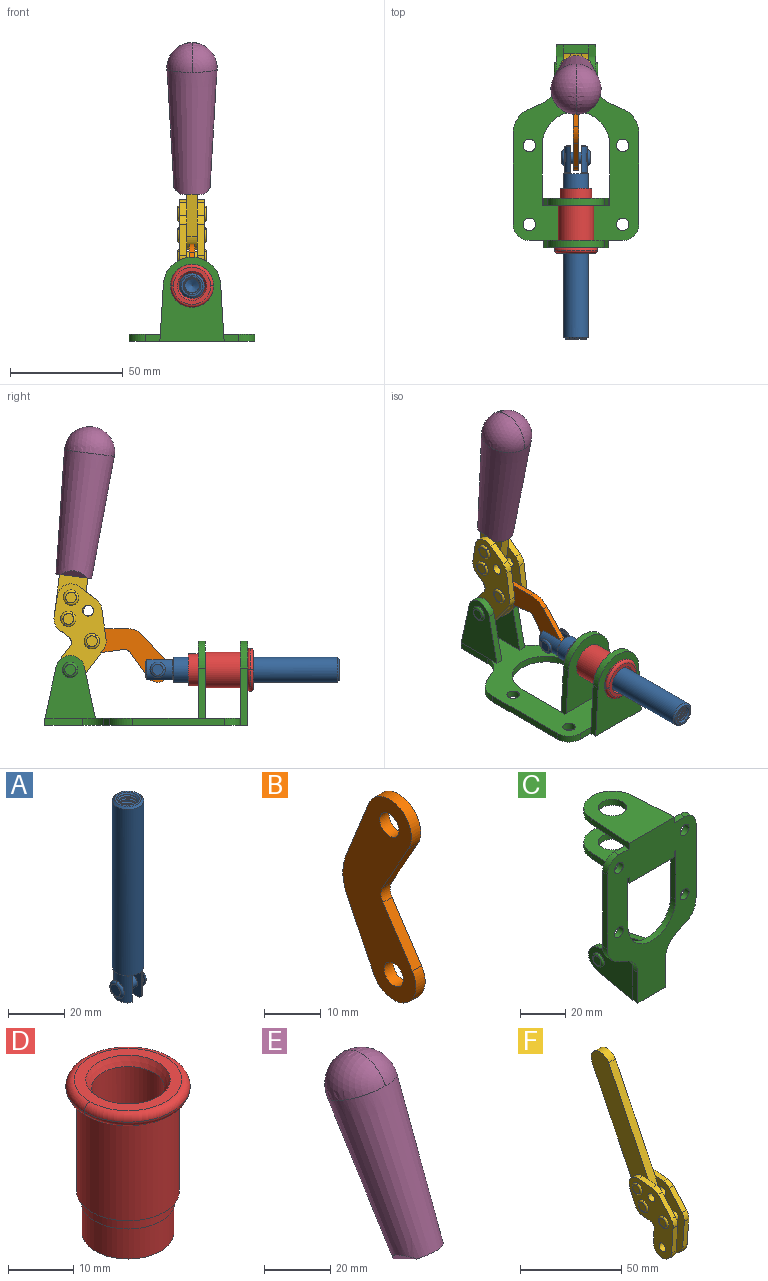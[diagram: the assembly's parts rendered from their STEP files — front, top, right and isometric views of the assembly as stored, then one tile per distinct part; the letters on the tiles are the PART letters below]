
ASSEMBLY  parts=6 mates=6
PART A: 48 faces, bbox 12.6x11.1x86.1 mm
  f0: torus R=2.41mm, axis (-1,0,0), area 15mm2, adj f30,f32,f34
  f1: torus R=2.41mm, axis (-1,0,0), area 15mm2, adj f29,f31,f33
  f2: cylinder r=5.54mm len=72.39mm, axis (0,0,1), area 2518.5mm2, adj f3,f4,f42,f43
  f3: cone r=5.54mm half-angle=45deg, axis (0,0,1), area 7.6mm2, adj f2,f5,f41
  f4: cone r=5.54mm half-angle=45deg, axis (0,0,-1), area 34.9mm2, adj f2,f39
  f5: cylinder r=5.08mm len=11.48mm, axis (0,0,1), area 108.3mm2, adj f3,f7,f8,f41
  f6: cylinder r=2.41mm len=4.83mm, axis (-1,0,0), area 71.2mm2, adj f40,f41
  f7: cylinder r=2.41mm len=4.83mm, axis (-1,0,0), area 7.6mm2, adj f5,f34
  f8: cone r=5.08mm half-angle=45deg, axis (0,0,1), area 10.6mm2, adj f5,f37,f41
  f9: cone r=3.98mm half-angle=45deg, axis (0,0,1), area 17.6mm2, adj f27,f39,f45,f46,f47
  f10: cylinder r=2.41mm len=4.83mm, axis (-1,0,0), area 7.6mm2, adj f33,f38
  f11: cylinder r=3.2mm len=6.4mm, axis (0,0,1), area 78.4mm2, adj f12,f28,f44,f45,f47
  f12: cylinder r=3.2mm len=6.4mm, axis (0,0,1), area 10.5mm2, adj f11,f13,f45,f47
  f13: cylinder r=3.2mm len=6.4mm, axis (0,0,1), area 10.5mm2, adj f12,f14,f45,f47
  f14: cylinder r=3.2mm len=6.4mm, axis (0,0,1), area 10.5mm2, adj f13,f15,f45,f47
  f15: cylinder r=3.2mm len=6.4mm, axis (0,0,1), area 10.5mm2, adj f14,f16,f45,f47
  f16: cylinder r=3.2mm len=6.4mm, axis (0,0,1), area 10.5mm2, adj f15,f17,f45,f47
  f17: cylinder r=3.2mm len=6.4mm, axis (0,0,1), area 10.5mm2, adj f16,f18,f45,f47
  f18: cylinder r=3.2mm len=6.4mm, axis (0,0,1), area 10.5mm2, adj f17,f19,f45,f47
  f19: cylinder r=3.2mm len=6.4mm, axis (0,0,1), area 10.5mm2, adj f18,f20,f45,f47
  f20: cylinder r=3.2mm len=6.4mm, axis (0,0,1), area 10.5mm2, adj f19,f21,f45,f47
  f21: cylinder r=3.2mm len=6.4mm, axis (0,0,1), area 10.5mm2, adj f20,f22,f45,f47
  f22: cylinder r=3.2mm len=6.4mm, axis (0,0,1), area 10.5mm2, adj f21,f23,f45,f47
  f23: cylinder r=3.2mm len=6.4mm, axis (0,0,1), area 10.5mm2, adj f22,f24,f45,f47
  f24: cylinder r=3.2mm len=6.4mm, axis (0,0,1), area 10.5mm2, adj f23,f25,f45,f47
  f25: cylinder r=3.2mm len=6.4mm, axis (0,0,1), area 10.5mm2, adj f24,f26,f45,f47
  f26: cylinder r=3.2mm len=6.4mm, axis (0,0,1), area 10.5mm2, adj f25,f27,f45,f47
  f27: cylinder r=3.2mm len=6.4mm, axis (0,0,1), area 7.4mm2, adj f9,f26,f45,f47
  f28: cone r=3.2mm half-angle=60deg, axis (0,0,1), area 37.2mm2, adj f11
  f29: plane 4.83x4.83mm, normal (-1,0,0), area 18.3mm2, adj f1,f31
  f30: plane 4.83x4.83mm, normal (1,0,0), area 18.3mm2, adj f0,f32
  f31: torus R=2.41mm, axis (-1,0,0), area 15mm2, adj f1,f29,f33
  f32: torus R=2.41mm, axis (-1,0,0), area 15mm2, adj f0,f30,f34
  f33: plane 6.83x6.83mm, normal (1,0,0), area 18.3mm2, adj f1,f10,f31
  f34: plane 6.83x6.83mm, normal (-1,0,0), area 18.3mm2, adj f0,f7,f32
  f35: cone r=5.08mm half-angle=45deg, axis (0,0,1), area 10.6mm2, adj f36,f38,f40
  f36: plane 7.25x1.97mm, normal (0,0,-1), area 10mm2, adj f35,f40
  f37: plane 7.25x1.97mm, normal (0,0,-1), area 10mm2, adj f8,f41
  f38: cylinder r=5.08mm len=11.48mm, axis (0,0,1), area 108.3mm2, adj f10,f35,f40,f42
  f39: plane 9.55x9.55mm, normal (0,0,1), area 22mm2, adj f4,f9
  f40: plane 12.76x10.09mm, normal (1,0,0), area 95.7mm2, adj f6,f35,f36,f38,f42,f43
  f41: plane 12.76x10.09mm, normal (-1,0,0), area 95.7mm2, adj f3,f5,f6,f8,f37,f43
  f42: cone r=5.54mm half-angle=45deg, axis (0,0,1), area 7.6mm2, adj f2,f38,f40
  f43: plane 11.07x4.7mm, normal (0,0,-1), area 50.4mm2, adj f2,f40,f41
  f44: plane 0.89x0.62mm, normal (-1,0,0), area 0.3mm2, adj f11,f45,f46,f47
  f45: bspline ~24.8x7.63mm, area 266.6mm2, adj f9,f11,f12,f13,f14,f15,f16,f17
  f46: bspline ~24.87x7.63mm, area 73.6mm2, adj f9,f44,f45,f47
  f47: bspline ~24.98x7.63mm, area 272.5mm2, adj f9,f11,f12,f13,f14,f15,f16,f17
PART B: 12 faces, bbox 2.3x18.2x42.8 mm
  f0: cylinder r=2.4mm len=4.8mm, axis (1,0,0), area 34.9mm2, adj f4,f11
  f1: cylinder r=10.41mm len=8.47mm, axis (1,0,0), area 20.2mm2, adj f4,f9,f10,f11
  f2: cylinder r=3.05mm len=3.16mm, axis (1,0,0), area 7.7mm2, adj f4,f6,f7,f11
  f3: cylinder r=2.4mm len=4.8mm, axis (1,0,0), area 34.9mm2, adj f4,f11
  f4: plane 42.81x18.23mm, normal (-1,0,0), area 414.1mm2, adj f0,f1,f2,f3,f5,f6,f7,f8
  f5: cylinder r=5.54mm len=10.67mm, axis (1,0,0), area 41.8mm2, adj f4,f6,f10,f11
  f6: plane 11.66x6.53mm, normal (0,-0.87,-0.49), area 30.9mm2, adj f2,f4,f5,f11
  f7: plane 11.17x7.33mm, normal (0,-0.84,0.55), area 30.9mm2, adj f2,f4,f8,f11
  f8: cylinder r=5.54mm len=10.51mm, axis (1,0,0), area 41.8mm2, adj f4,f7,f9,f11
  f9: plane 13.67x6.67mm, normal (0,0.9,-0.44), area 35.1mm2, adj f1,f4,f8,f11
  f10: plane 14.1x5.7mm, normal (0,0.93,0.37), area 35.1mm2, adj f1,f4,f5,f11
  f11: plane 42.81x18.23mm, normal (1,0,0), area 414.1mm2, adj f0,f1,f2,f3,f5,f6,f7,f8
PART C: 55 faces, bbox 55.7x37.4x89.8 mm
  f0: torus R=2.41mm, axis (-1,0,0), area 15mm2, adj f11,f15,f25
  f1: torus R=2.41mm, axis (-1,0,0), area 15mm2, adj f10,f12,f22
  f2: cylinder r=2.78mm len=5.56mm, axis (0,-1,0), area 54.2mm2, adj f30,f54
  f3: cylinder r=14.99mm len=29.97mm, axis (0,-1,0), area 145.9mm2, adj f30,f49,f53,f54
  f4: cylinder r=2.78mm len=5.56mm, axis (0,-1,0), area 54.2mm2, adj f30,f54
  f5: cylinder r=2.78mm len=5.56mm, axis (0,-1,0), area 54.2mm2, adj f30,f54
  f6: cylinder r=2.78mm len=5.56mm, axis (0,-1,0), area 54.2mm2, adj f30,f54
  f7: cylinder r=6.35mm len=12.7mm, axis (0,0,1), area 123.6mm2, adj f27,f51
  f8: cylinder r=6.35mm len=12.7mm, axis (0,0,-1), area 124.7mm2, adj f21,f35
  f9: cylinder r=2.41mm len=11.18mm, axis (-1,0,0), area 169.4mm2, adj f16,f19
  f10: plane 4.83x4.83mm, normal (1,0,0), area 18.3mm2, adj f1,f12
  f11: plane 4.83x4.83mm, normal (-1,0,0), area 18.3mm2, adj f0,f15
  f12: torus R=2.41mm, axis (-1,0,0), area 15mm2, adj f1,f10,f22
  f13: cylinder r=6.35mm len=12.41mm, axis (1,0,0), area 53.4mm2, adj f18,f19,f22,f23
  f14: cylinder r=6.35mm len=12.41mm, axis (-1,0,0), area 53.4mm2, adj f16,f17,f24,f25
  f15: torus R=2.41mm, axis (-1,0,0), area 15mm2, adj f0,f11,f25
  f16: plane 27.86x22.35mm, normal (1,0,0), area 425.4mm2, adj f9,f14,f17,f24,f30
  f17: plane 22.86x4.97mm, normal (0,0.21,0.98), area 72.5mm2, adj f14,f16,f25,f30
  f18: plane 22.86x4.97mm, normal (0,0.21,0.98), area 72.5mm2, adj f13,f19,f22,f30
  f19: plane 27.86x22.35mm, normal (-1,0,0), area 425.4mm2, adj f9,f13,f18,f23,f30
  f20: cylinder r=12.7mm len=25.35mm, axis (0,0,-1), area 119.8mm2, adj f21,f34,f35,f36
  f21: plane 34.21x28.07mm, normal (0,0,-1), area 702.4mm2, adj f8,f20,f30,f34,f36
  f22: plane 27.96x22.45mm, normal (1,0,0), area 407.2mm2, adj f1,f12,f13,f18,f23,f30,f42,f43
  f23: plane 22.86x4.97mm, normal (0,0.21,-0.98), area 72.5mm2, adj f13,f19,f22,f44
  f24: plane 22.86x4.97mm, normal (0,0.21,-0.98), area 72.5mm2, adj f14,f16,f25,f44
  f25: plane 27.86x22.35mm, normal (-1,0,0), area 407.1mm2, adj f0,f14,f15,f17,f24,f30,f45,f46
  f26: plane 3.1x0.95mm, normal (0,0,-1), area 2.7mm2, adj f30,f49,f50,f54
  f27: plane 34.21x28.07mm, normal (0,0,1), area 702.4mm2, adj f7,f28,f30,f50,f52
  f28: cylinder r=12.7mm len=25.35mm, axis (0,0,1), area 118.8mm2, adj f27,f50,f51,f52
  f29: plane 3.1x0.95mm, normal (0,0,-1), area 2.7mm2, adj f30,f52,f53,f54
  f30: plane 86.54x55.63mm, normal (0,1,0), area 2362.9mm2, adj f2,f3,f4,f5,f6,f16,f17,f18
  f31: plane 40.56x3.1mm, normal (-1,0,0), area 125.7mm2, adj f30,f32,f48,f54
  f32: cylinder r=7.11mm len=7.11mm, axis (0,-1,0), area 34.6mm2, adj f30,f31,f33,f54
  f33: plane 6.67x3.1mm, normal (0,0,1), area 20.4mm2, adj f30,f32,f34,f54
  f34: plane 25.39x3.13mm, normal (-1,0.06,0), area 79.5mm2, adj f20,f21,f33,f35,f54
  f35: plane 37.31x28.45mm, normal (0,0,1), area 789.9mm2, adj f8,f20,f34,f36,f54
  f36: plane 25.39x3.13mm, normal (1,0.06,0), area 79.5mm2, adj f20,f21,f35,f37,f54
  f37: plane 6.67x3.1mm, normal (0,0,1), area 20.4mm2, adj f30,f36,f38,f54
  f38: cylinder r=7.11mm len=7.11mm, axis (0,-1,0), area 34.6mm2, adj f30,f37,f39,f54
  f39: plane 40.56x3.1mm, normal (1,0,0), area 125.7mm2, adj f30,f38,f40,f54
  f40: cylinder r=11.18mm len=10.16mm, axis (0,-1,0), area 39.5mm2, adj f30,f39,f41,f54
  f41: plane 6.09x3.1mm, normal (0.42,0,-0.91), area 20.8mm2, adj f30,f40,f42,f54
  f42: cylinder r=11.18mm len=9.41mm, axis (0,-1,0), area 37.2mm2, adj f22,f30,f41,f43,f54
  f43: plane 16.5x3.1mm, normal (1,0,0), area 51.1mm2, adj f22,f42,f44,f54
  f44: plane 17.37x3.1mm, normal (0,0,-1), area 53.8mm2, adj f23,f24,f30,f43,f45,f54
  f45: plane 16.5x3.1mm, normal (-1,0,0), area 51.1mm2, adj f25,f44,f46,f54
  f46: cylinder r=11.18mm len=9.41mm, axis (0,-1,0), area 37.2mm2, adj f25,f30,f45,f47,f54
  f47: plane 6.09x3.1mm, normal (-0.42,0,-0.91), area 20.8mm2, adj f30,f46,f48,f54
  f48: cylinder r=11.18mm len=10.16mm, axis (0,-1,0), area 39.5mm2, adj f30,f31,f47,f54
  f49: plane 26.54x3.1mm, normal (-1,0,0), area 82.3mm2, adj f3,f26,f30,f54
  f50: plane 25.39x3.1mm, normal (1,0.06,0), area 78.8mm2, adj f26,f27,f28,f51,f54
  f51: plane 37.31x28.45mm, normal (0,0,-1), area 789.9mm2, adj f7,f28,f50,f52,f54
  f52: plane 25.39x3.1mm, normal (-1,0.06,0), area 78.8mm2, adj f27,f28,f29,f51,f54
  f53: plane 26.54x3.1mm, normal (1,0,0), area 82.3mm2, adj f3,f29,f30,f54
  f54: plane 89.66x55.63mm, normal (0,-1,0), area 2678.5mm2, adj f2,f3,f4,f5,f6,f26,f29,f31
PART D: 15 faces, bbox 20.6x20.6x28.7 mm
  f0: torus R=8.26mm, axis (0,0,1), area 56.8mm2, adj f1,f10,f12
  f1: torus R=8.26mm, axis (0,0,1), area 56.8mm2, adj f0,f6,f13
  f2: cylinder r=5.59mm len=25.91mm, axis (0,0,1), area 909.6mm2, adj f3,f4
  f3: cone r=6.86mm half-angle=45deg, axis (0,0,-1), area 70.2mm2, adj f2,f14
  f4: cone r=6.47mm half-angle=30deg, axis (0,0,1), area 66.7mm2, adj f2,f13
  f5: cylinder r=7.04mm len=14.07mm, axis (0,0,1), area 252.6mm2, adj f11,f14
  f6: torus R=8.26mm, axis (0,0,1), area 56.8mm2, adj f1,f12,f13
  f7: cylinder r=7.16mm len=14.33mm, axis (0,0,1), area 91.5mm2, adj f9,f11
  f8: cylinder r=7.86mm len=18.42mm, axis (0,0,1), area 909.6mm2, adj f9,f10
  f9: plane 15.72x15.72mm, normal (0,0,-1), area 33mm2, adj f7,f8
  f10: plane 16.51x16.51mm, normal (0,0,-1), area 19.9mm2, adj f0,f8,f12
  f11: plane 14.33x14.33mm, normal (0,0,-1), area 5.7mm2, adj f5,f7
  f12: torus R=8.26mm, axis (0,0,1), area 56.8mm2, adj f0,f6,f10
  f13: plane 16.51x16.51mm, normal (0,0,1), area 82.7mm2, adj f1,f4,f6
  f14: plane 14.07x14.07mm, normal (0,0,-1), area 7.8mm2, adj f3,f5
PART E: 11 faces, bbox 22.3x42.6x64.5 mm
  f0: sphere r=11.13mm, area 411.4mm2, adj f1,f8
  f1: cone r=11.11mm half-angle=3.3deg, axis (0,0.44,0.9), area 3251.8mm2, adj f0,f7,f8,f9,f10
  f2: cylinder r=6.16mm len=11.7mm, axis (1,0,0), area 89.5mm2, adj f3,f4,f5,f6
  f3: plane 60.23x36.75mm, normal (-1,0,0), area 763.6mm2, adj f2,f4,f6,f10
  f4: plane 51.37x25.05mm, normal (0,0.9,-0.44), area 264.2mm2, adj f2,f3,f5,f10
  f5: plane 60.23x36.75mm, normal (1,0,0), area 763.6mm2, adj f2,f4,f6,f10
  f6: plane 51.37x25.05mm, normal (0,-0.9,0.44), area 264.2mm2, adj f2,f3,f5,f10
  f7: plane 9.95x5.95mm, normal (0.71,-0.31,-0.64), area 25.8mm2, adj f1,f10
  f8: sphere r=11.13mm, area 411.4mm2, adj f0,f1
  f9: plane 9.95x5.95mm, normal (-0.71,-0.31,-0.64), area 25.8mm2, adj f1,f10
  f10: plane 14.27x11.38mm, normal (0,-0.44,-0.9), area 106.7mm2, adj f1,f3,f4,f5,f6,f7,f9
PART F: 59 faces, bbox 12.9x60.2x99.6 mm
  f0: torus R=2.39mm, axis (-1,0,0), area 14.9mm2, adj f20,f43,f51
  f1: torus R=2.39mm, axis (-1,0,0), area 14.9mm2, adj f19,f42,f51
  f2: torus R=2.39mm, axis (-1,0,0), area 14.9mm2, adj f18,f35,f51
  f3: torus R=2.39mm, axis (-1,0,0), area 14.9mm2, adj f14,f17,f23
  f4: torus R=2.39mm, axis (-1,0,0), area 14.9mm2, adj f13,f16,f23
  f5: torus R=2.39mm, axis (-1,0,0), area 14.9mm2, adj f12,f15,f23
  f6: cylinder r=2.39mm len=4.78mm, axis (1,0,0), area 46.5mm2, adj f48,f50,f51
  f7: cylinder r=2.39mm len=4.78mm, axis (1,0,0), area 46.5mm2, adj f50,f51
  f8: cylinder r=6.35mm len=12.68mm, axis (1,0,0), area 61.8mm2, adj f38,f39,f50,f51
  f9: cylinder r=2.39mm len=4.78mm, axis (-1,0,0), area 70.5mm2, adj f46,f50
  f10: cylinder r=2.39mm len=4.78mm, axis (-1,0,0), area 46.5mm2, adj f23,f45,f46
  f11: cylinder r=2.39mm len=4.78mm, axis (-1,0,0), area 46.5mm2, adj f23,f46
  f12: plane 4.78x4.78mm, normal (1,0,0), area 17.9mm2, adj f5,f15
  f13: plane 4.78x4.78mm, normal (1,0,0), area 17.9mm2, adj f4,f16
  f14: plane 4.78x4.78mm, normal (1,0,0), area 17.9mm2, adj f3,f17
  f15: torus R=2.39mm, axis (-1,0,0), area 14.9mm2, adj f5,f12,f23
  f16: torus R=2.39mm, axis (-1,0,0), area 14.9mm2, adj f4,f13,f23
  f17: torus R=2.39mm, axis (-1,0,0), area 14.9mm2, adj f3,f14,f23
  f18: plane 4.78x4.78mm, normal (-1,0,0), area 17.9mm2, adj f2,f35
  f19: plane 4.78x4.78mm, normal (-1,0,0), area 17.9mm2, adj f1,f42
  f20: plane 4.78x4.78mm, normal (-1,0,0), area 17.9mm2, adj f0,f43
  f21: plane 2.26x0.2mm, normal (1,0,0), area 0.2mm2, adj f31,f44
  f22: plane 2.26x0.2mm, normal (-1,0,0), area 0.2mm2, adj f41,f44
  f23: plane 39.37x30.77mm, normal (1,0,0), area 565.5mm2, adj f3,f4,f5,f10,f11,f15,f16,f17
  f24: cylinder r=6.1mm len=4.15mm, axis (-1,0,0), area 14.7mm2, adj f23,f25,f32,f46
  f25: plane 10.25x9.01mm, normal (0,-0.75,0.66), area 42.3mm2, adj f23,f24,f26,f46
  f26: cylinder r=6.35mm len=4.64mm, axis (-1,0,0), area 15.6mm2, adj f23,f25,f27,f46
  f27: plane 15.84x3.1mm, normal (0,-1,-0.07), area 49.2mm2, adj f23,f26,f28,f46
  f28: cylinder r=6.35mm len=12.68mm, axis (-1,0,0), area 61.8mm2, adj f23,f27,f29,f46
  f29: plane 8.11x3.1mm, normal (0,1,0.07), area 25.2mm2, adj f23,f28,f30,f46
  f30: cylinder r=3.05mm len=3.25mm, axis (-1,0,0), area 14.8mm2, adj f23,f29,f31,f46
  f31: plane 5.99x3.1mm, normal (0,0.07,-1), area 18.6mm2, adj f21,f23,f30,f44,f46
  f32: plane 9.5x3.1mm, normal (0,-0.07,1), area 29.5mm2, adj f23,f24,f33,f46,f47
  f33: cylinder r=6.1mm len=8.63mm, axis (-1,0,0), area 39.1mm2, adj f23,f32,f34,f47
  f34: plane 8.65x3.96mm, normal (0,0.91,-0.42), area 29.5mm2, adj f23,f33,f44,f47
  f35: torus R=2.39mm, axis (-1,0,0), area 14.9mm2, adj f2,f18,f51
  f36: plane 10.25x9.01mm, normal (0,-0.75,0.66), area 42.3mm2, adj f37,f49,f50,f51
  f37: cylinder r=6.35mm len=4.64mm, axis (1,0,0), area 15.6mm2, adj f36,f38,f50,f51
  f38: plane 15.84x3.1mm, normal (0,-1,-0.07), area 49.2mm2, adj f8,f37,f50,f51
  f39: plane 8.11x3.1mm, normal (0,1,0.07), area 25.2mm2, adj f8,f40,f50,f51
  f40: cylinder r=3.05mm len=3.25mm, axis (1,0,0), area 14.8mm2, adj f39,f41,f50,f51
  f41: plane 5.99x3.1mm, normal (0,0.07,-1), area 18.6mm2, adj f22,f40,f44,f50,f51
  f42: torus R=2.39mm, axis (-1,0,0), area 14.9mm2, adj f1,f19,f51
  f43: torus R=2.39mm, axis (-1,0,0), area 14.9mm2, adj f0,f20,f51
  f44: cylinder r=6.35mm len=12.12mm, axis (-1,0,0), area 128.9mm2, adj f21,f22,f23,f31,f34,f41,f46,f47
  f45: plane 2.65x1.35mm, normal (1,0,0), area 1mm2, adj f10,f55
  f46: plane 39.08x20.42mm, normal (-1,0,0), area 412.5mm2, adj f9,f10,f11,f24,f25,f26,f27,f28
  f47: plane 77.62x39.82mm, normal (1,0,0), area 850mm2, adj f32,f33,f34,f44,f53,f54,f55
  f48: plane 2.65x1.35mm, normal (-1,0,0), area 1mm2, adj f6,f55
  f49: cylinder r=6.1mm len=4.15mm, axis (1,0,0), area 14.7mm2, adj f36,f50,f51,f56
  f50: plane 39.08x20.42mm, normal (1,0,0), area 412.5mm2, adj f6,f7,f8,f9,f36,f37,f38,f39
  f51: plane 39.37x30.77mm, normal (-1,0,0), area 565.5mm2, adj f0,f1,f2,f6,f7,f8,f35,f36
  f52: plane 8.65x3.96mm, normal (0,0.91,-0.42), area 29.5mm2, adj f44,f51,f57,f58
  f53: plane 68.49x33.4mm, normal (0,0.9,-0.44), area 358.1mm2, adj f44,f47,f54,f58
  f54: cylinder r=6.35mm len=12.06mm, axis (1,0,0), area 93.7mm2, adj f47,f53,f55,f58
  f55: plane 68.49x33.4mm, normal (0,-0.9,0.44), area 358.1mm2, adj f44,f45,f46,f47,f48,f50,f54,f58
  f56: plane 9.5x3.1mm, normal (0,-0.07,1), area 29.5mm2, adj f49,f50,f51,f57,f58
  f57: cylinder r=6.1mm len=8.63mm, axis (1,0,0), area 39.1mm2, adj f51,f52,f56,f58
  f58: plane 77.62x39.82mm, normal (-1,0,0), area 850mm2, adj f44,f52,f53,f54,f55,f56,f57
PLACE A rot(axis=(1,0,0),90deg) t=(0,18.27,0)mm
PLACE B rot(axis=(1,0,0),115.5deg) t=(0,27.34,9.04)mm
PLACE C rot(axis=(1,0,0),90deg) t=(0,9.43,0)mm fixed
PLACE D rot(axis=(1,0,0),90deg) t=(0,9.43,0)mm
PLACE E rot(axis=(1,0,0),33.2deg) t=(0,3.35,37.97)mm
PLACE F rot(axis=(1,0,0),33.2deg) t=(0,3.35,37.97)mm
MATE slider A.f2 <-> C.f7  axis (0,-1,0) through (0,-40.52,24.61)mm
MATE fastened E.f2 <-> F.f54  axis (1,0,0) through (0,32.75,122.72)mm
MATE revolute B.f3 <-> F.f4  axis (1,0,0) through (0,31.92,37.25)mm
MATE revolute F.f7 <-> C.f0  axis (1,0,0) through (0,41.52,24.61)mm
MATE revolute A.f6 <-> B.f5  axis (-1,0,0) through (0,2.79,24.61)mm
MATE fastened C.f7 <-> D.f0  axis (0,-1,0) through (0,-36.96,24.61)mm
